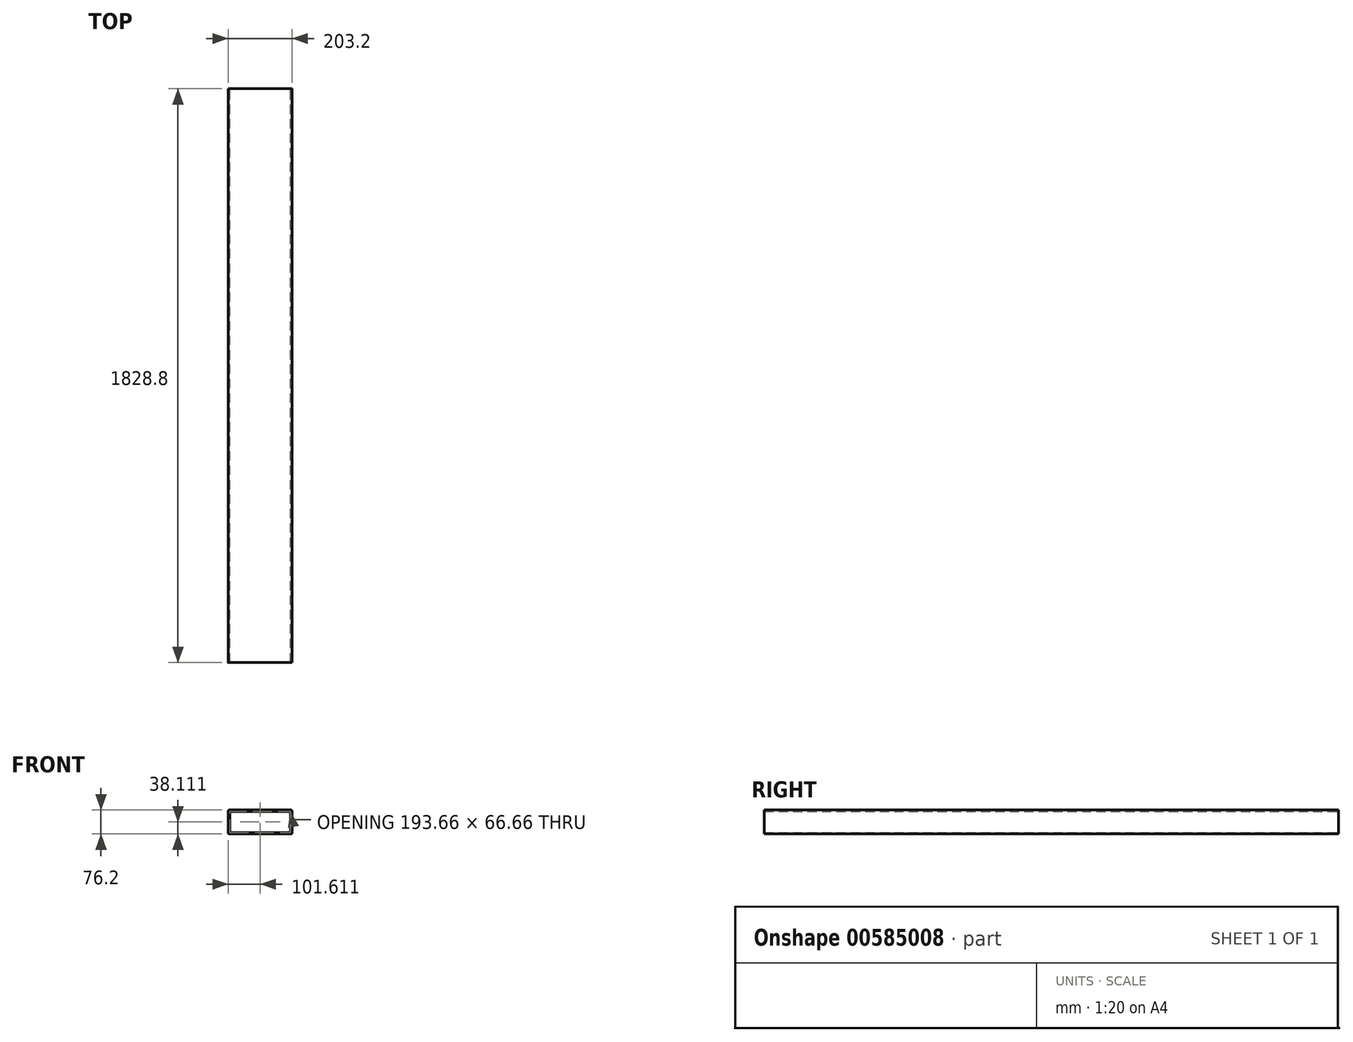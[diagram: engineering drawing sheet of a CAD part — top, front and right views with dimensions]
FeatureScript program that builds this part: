
annotation { "Feature Type Name" : "Feature", "Feature Type Description" : "" }
export const myFeature = defineFeature(function(context is Context, id is Id, definition is map)
    precondition{}
    {
        {
            var Q0;
            Q0=qCreatedBy(makeId("Front.planeOp"),FACE);
            var sketch = newSketch(context, id + "F0", { "sketchPlane" : qUnion([Q0])});
            skLineSegment(sketch, "E0.bottom", {"start": v(0, 0) * mm, "end": v(193.66, 0) * mm});
            skLineSegment(sketch, "E0.top", {"start": v(0, 66.66) * mm, "end": v(193.66, 66.66) * mm});
            skLineSegment(sketch, "E0.left", {"start": v(0, 0) * mm, "end": v(0, 66.66) * mm});
            skLineSegment(sketch, "E0.right", {"start": v(193.66, 0) * mm, "end": v(193.66, 66.66) * mm});
            skLineSegment(sketch, "E1.bottom", {"start": v(-4.78, -4.78) * mm, "end": v(198.42, -4.78) * mm});
            skLineSegment(sketch, "E1.top", {"start": v(-4.78, 71.42) * mm, "end": v(198.42, 71.42) * mm});
            skLineSegment(sketch, "E1.left", {"start": v(-4.78, -4.78) * mm, "end": v(-4.78, 71.42) * mm});
            skLineSegment(sketch, "E1.right", {"start": v(198.42, -4.78) * mm, "end": v(198.42, 71.42) * mm});
            skLineSegment(sketch, "E2", {"start": v(193.66, 66.66) * mm, "end": v(198.42, 66.66) * mm});
            skLineSegment(sketch, "E3", {"start": v(198.42, 66.66) * mm, "end": v(198.42, 71.42) * mm});
            skSolve(sketch);
        }
        {
            var Q0;
            Q0=makeQuery(id+"F0.imprint","IMPRINT",FACE,{"disambiguationData":[TD([[makeQuery(id+"F0.imprint","IMPRINT",EDGE,{"derivedFrom":sQuery(id+"F0.wireOp",EDGE,"E0.bottom")}),-1.0]])]});
            extrude(context, id + "F1", {"entities" : qUnion([Q0]), "depth" : 1828.8 * mm, "offsetDistance" : 25.4 * mm, "symmetric" : true});
        }
        {
            var Q0;
            Q0=makeQuery(id+"F1.opExtrude","SWEPT_EDGE",EDGE,{"disambiguationData":[OSD([sQuery(id+"F0.wireOp",EDGE,"E1.top"),sQuery(id+"F0.wireOp",EDGE,"E1.left")])]});
            var Q1;
            Q1=makeQuery(id+"F1.opExtrude","SWEPT_EDGE",EDGE,{"disambiguationData":[OSD([sQuery(id+"F0.wireOp",EDGE,"E0.top"),sQuery(id+"F0.wireOp",EDGE,"E0.left")])]});
            var Q2;
            Q2=makeQuery(id+"F1.opExtrude","SWEPT_EDGE",EDGE,{"disambiguationData":[OSD([sQuery(id+"F0.wireOp",EDGE,"E1.bottom"),sQuery(id+"F0.wireOp",EDGE,"E1.left")])]});
            var Q3;
            Q3=makeQuery(id+"F1.opExtrude","SWEPT_EDGE",EDGE,{"disambiguationData":[OSD([sQuery(id+"F0.wireOp",EDGE,"E1.bottom"),sQuery(id+"F0.wireOp",EDGE,"E1.right")])]});
            var Q4;
            Q4=makeQuery(id+"F1.opExtrude","SWEPT_EDGE",EDGE,{"disambiguationData":[OSD([sQuery(id+"F0.wireOp",EDGE,"E1.top"),sQuery(id+"F0.wireOp",EDGE,"E3")])]});
            var Q5;
            Q5=makeQuery(id+"F1.opExtrude","SWEPT_EDGE",EDGE,{"disambiguationData":[OSD([sQuery(id+"F0.wireOp",EDGE,"E0.bottom"),sQuery(id+"F0.wireOp",EDGE,"E0.right")])]});
            var Q6;
            Q6=makeQuery(id+"F1.opExtrude","SWEPT_EDGE",EDGE,{"disambiguationData":[OSD([sQuery(id+"F0.wireOp",EDGE,"E0.top"),sQuery(id+"F0.wireOp",EDGE,"E0.right")])]});
            fillet(context, id + "F2", {"entities" : qUnion([Q0, Q1, Q2, Q3, Q4, Q5, Q6]), "radius" : 3.17 * mm, "tangentPropagation" : true, "allowEdgeOverflow" : false});
        }
    });
